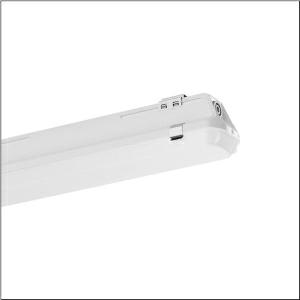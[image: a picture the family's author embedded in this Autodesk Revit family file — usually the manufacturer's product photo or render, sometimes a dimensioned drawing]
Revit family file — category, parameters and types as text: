
# Revit family: monsun_r__21_parking_51fg20dp440bhr_9634
name_source: partatom
category: Lighting Fixtures
units: mm (PartAtom-declared; Revit-internal decimal feet)

## family parameters
Cut with Voids When Loaded = No
Host = Face
Light Source = No
Part Type = Normal
Room Calculation Point = No
Round Connector Dimension = Use Diameter
Shared = No

## types (1)
- --- (1 x LED, 4810 lm, 34.9 W, 4000K)
    Apparent Load = 35 VA
    CIE Flux Codes = 45 75 93 94 100
    Color Rendering = 80
    Color Temperature = 4000K
    Default Elevation = 1800 mm
    Description = Monsun® 21 parking, damp-proof luminaire, chain hanger, primary optical cover: enclosure, of PC, light emission: direct distribution, primary light characteristic: symmetric, installation type: vertical mounting, horizontal mounting, surface-mounted, suspended mounting, LED, rated luminous flux: 4.810lm, luminous efficacy: 140lm/W, light colour: 840, colour temperature: 4000K, control gear: ECG DALI, with terminal, 5-pole, max. 2.5mm², mains connection: 220..240V, AC, 50/60Hz, rated input power: 34W, housing, of glass-fibre reinforced polyester, uncoated, bright grey, incl. chain hanger, length: 1.590mm, width: 90mm, height: 88mm, clip for enclosure, of stainless steel (V2A), ceiling mounting element, of stainless steel (V2A), chain hanger, of stainless steel (V2A), multi-sensor HC1, local control, light sensor deactivated, dimmable, protection rating (complete): IP66, insulation class (complete): insulation class I (protective earthing), certification: CE, ENEC, VDE, UKCA, protection symbol: D, impact resistance: IK08, permissible operating ambient temperature: -25..+35°C, standard: EN 50419, EN 60598-2-1, no direct snow, no direct sun, no direct rain, for indoor or canopied outdoor use, corresponds to IFS (International Featured Standards) requirements for safety and quality in the food industry, contact your sales advisor before using the luminaires in applications with unclear chemical exposure, large temperature fluctuations or condensation-forming humidity, LABS conformity tested according to VDMA 24364:2018-05, packaging unit: 1 piece
    Height = 89 mm
    Lamp = 1 x LED
    Lamp Light Flux = 4810 lm
    Lamp Power = 34.9 W
    Lamp count = 1
    Length = 1590 mm
    Luminous efficacy = 138 lm/W
    Manufacturer = Siteco
    ModVariant = No
    Model = 51FG20DP440BHR
    Mounting Place = Ceiling
    Mounting Type = Surface mounted
    Number of Poles = 1
    OnlyDefault = Yes
    Power Factor = 1
    Product Name = Monsun® 21 parking
    Product group = damp-proof luminaire
    ProductGroupID = 300
    Protection Class = Protection class I
    Protection Degree = IP 66
    RLX_Detail_Level = 1
    RLX_Emergency_Light_Flux = 0 lm
    RLX_Emergency_Type = 0
    RLX_Emergency_Type_DB = No
    RlxData = <blob elided: 92297 chars, md5=d0ec9c00>
    Socket = socket
    Standby Power = 0 W
    System Light Flux = 4810 lm
    System Power = 35 W
    Type Comments = factory setting: luminous flux: 100 % | dim-lin: 254 | 228 mA
    Type Image = l_1319656.jpg
    URL = http://relux.com
    VarID = @adj_113231
    Voltage = 0 V
    Weight = 0.00 kg
    Width = 90 mm

## geometry (parser evidence)
native form markers: Blend x4, Sweep x15
no freeform markers — native parametric forms only
